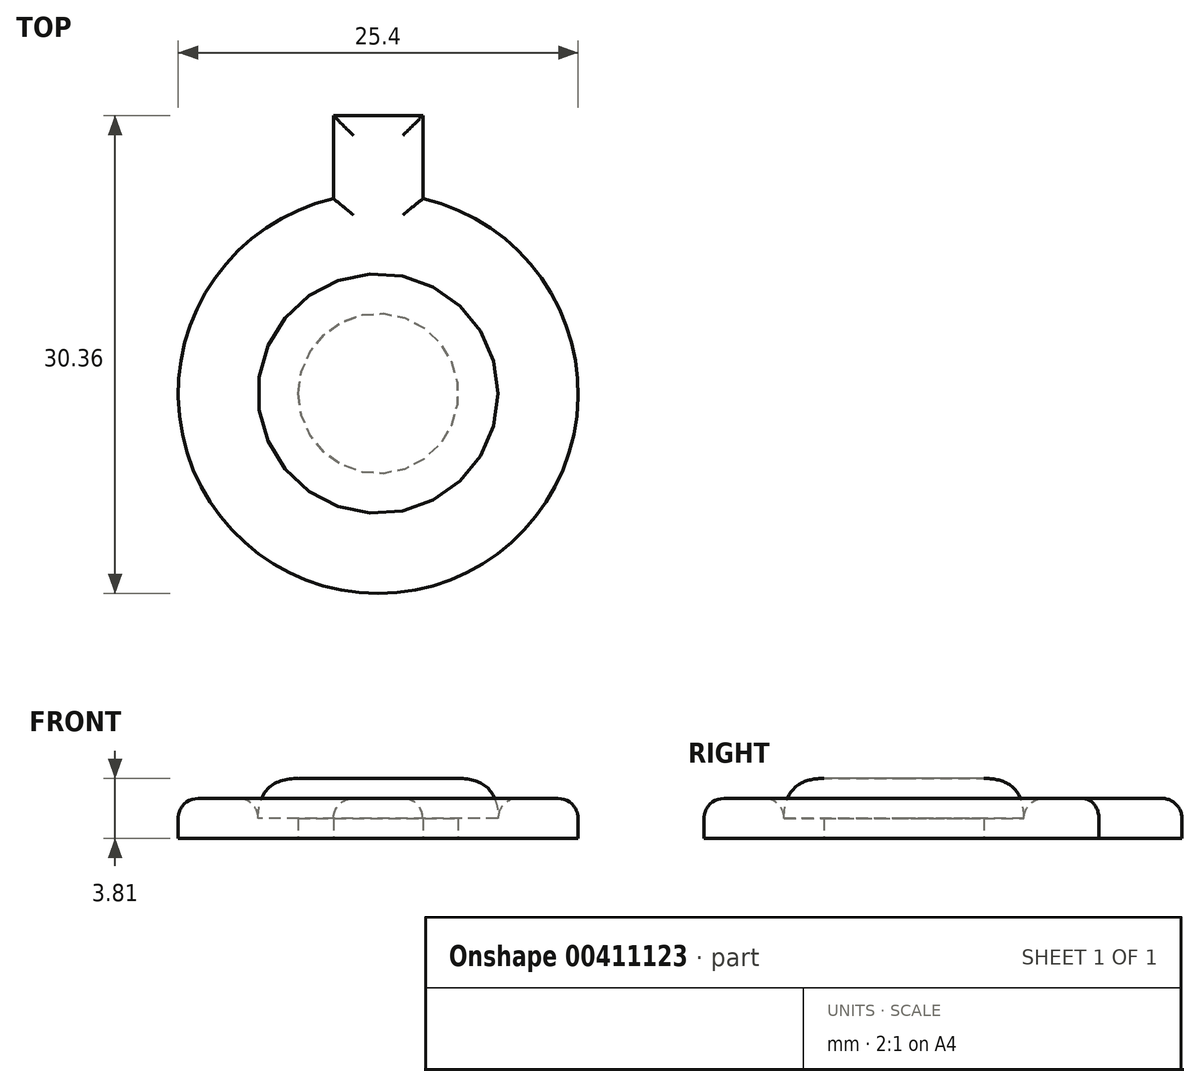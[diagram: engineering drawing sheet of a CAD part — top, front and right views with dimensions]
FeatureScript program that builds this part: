
annotation { "Feature Type Name" : "Feature", "Feature Type Description" : "" }
export const myFeature = defineFeature(function(context is Context, id is Id, definition is map)
    precondition{}
    {
        {
            var Q0;
            Q0=qCreatedBy(makeId("Top.planeOp"),FACE);
            var sketch = newSketch(context, id + "F0", { "sketchPlane" : qUnion([Q0])});
            skCircle(sketch, "E0", {"center": v(0, 0) * mm, "radius": 12.7 * mm});
            skCircle(sketch, "E1.0", {"center": v(0, 0) * mm, "radius": 7.62 * mm});
            skLineSegment(sketch, "E2.bottom", {"start": v(2.84, 17.66) * mm, "end": v(-2.84, 17.66) * mm});
            skLineSegment(sketch, "E2.top", {"start": v(2.84, 7.74) * mm, "end": v(-2.84, 7.74) * mm});
            skLineSegment(sketch, "E2.left", {"start": v(2.84, 17.66) * mm, "end": v(2.84, 7.74) * mm});
            skLineSegment(sketch, "E2.right", {"start": v(-2.84, 17.66) * mm, "end": v(-2.84, 7.74) * mm});
            skPoint(sketch, "E2.middle", {"position": v(0, 12.7) * mm});
            skSolve(sketch);
        }
        {
            var Q0;
            {var subQ5=sQuery(id+"F0.wireOp",EDGE,"E2.top");Q0=makeQuery(id+"F0.imprint","IMPRINT",FACE,{"disambiguationData":[TD([[makeQuery(id+"F0.imprint","IMPRINT",EDGE,{"derivedFrom":subQ5}),-1.0]])]});}
            var Q1;
            {var subQ5=sQuery(id+"F0.wireOp",EDGE,"E2.bottom");Q1=makeQuery(id+"F0.imprint","IMPRINT",FACE,{"disambiguationData":[TD([[makeQuery(id+"F0.imprint","IMPRINT",EDGE,{"derivedFrom":subQ5}),1.0]])]});}
            var Q2;
            Q2=makeQuery(id+"F0.imprint","IMPRINT",FACE,{"disambiguationData":[TD([[makeQuery(id+"F0.imprint","IMPRINT",EDGE,{"derivedFrom":sQuery(id+"F0.wireOp",EDGE,"E1.0")}),-1.0]])]});
            extrude(context, id + "F1", {"entities" : qUnion([Q0, Q1, Q2]), "depth" : 2.54 * mm});
        }
        {
            var Q0;
            Q0=makeQuery(id+"F1.opExtrude","CAP_EDGE",EDGE,{"disambiguationData":[OSD([sQuery(id+"F0.wireOp",EDGE,"E0")])],"isStart":false});
            var Q1;
            Q1=makeQuery(id+"F1.opExtrude","CAP_EDGE",EDGE,{"disambiguationData":[OSD([sQuery(id+"F0.wireOp",EDGE,"E2.left")])],"isStart":false});
            var Q2;
            Q2=makeQuery(id+"F1.opExtrude","CAP_EDGE",EDGE,{"disambiguationData":[OSD([sQuery(id+"F0.wireOp",EDGE,"E2.bottom")])],"isStart":false});
            var Q3;
            Q3=makeQuery(id+"F1.opExtrude","CAP_EDGE",EDGE,{"disambiguationData":[OSD([sQuery(id+"F0.wireOp",EDGE,"E2.right")])],"isStart":false});
            var Q4;
            Q4=makeQuery(id+"F1.opExtrude","CAP_EDGE",EDGE,{"disambiguationData":[OSD([sQuery(id+"F0.wireOp",EDGE,"E1.0")])],"isStart":false});
            fillet(context, id + "F2", {"entities" : qUnion([Q0, Q1, Q2, Q3, Q4]), "radius" : 1.27 * mm, "tangentPropagation" : true, "allowEdgeOverflow" : false});
        }
        {
            var Q0;
            Q0=makeQuery(id+"F0.imprint","IMPRINT",FACE,{"disambiguationData":[TD([[makeQuery(id+"F0.imprint","IMPRINT",EDGE,{"derivedFrom":sQuery(id+"F0.wireOp",EDGE,"E1.0")}),1.0]])]});
            extrude(context, id + "F3", {"entities" : qUnion([Q0]), "operationType" : NewBodyOperationType.ADD, "depth" : 3.8 * mm});
        }
        {
            var Q0;
            Q0=makeQuery(id+"F3.opExtrude","CAP_EDGE",EDGE,{"disambiguationData":[OSD([sQuery(id+"F0.wireOp",EDGE,"E1.0")])],"isStart":false});
            fillet(context, id + "F4", {"entities" : qUnion([Q0]), "radius" : 2.54 * mm, "tangentPropagation" : true, "rho" : 0.5, "crossSection" : FilletCrossSection.CONIC, "allowEdgeOverflow" : false});
        }
        {
            var Q0;
            {var subQ0=sQuery(id+"F0.wireOp",EDGE,"E1.0");Q0=makeQuery(id+"F3.boolean.opBoolean","MERGE",FACE,{"derivedFrom":[makeQuery(id+"F1.opExtrude","CAP_FACE",FACE,{"disambiguationData":[OSD([sQuery(id+"F0.wireOp",EDGE,"E0"),subQ0,sQuery(id+"F0.wireOp",EDGE,"E2.bottom"),sQuery(id+"F0.wireOp",EDGE,"E2.left"),sQuery(id+"F0.wireOp",EDGE,"E2.right")])],"isStart":true}),makeQuery(id+"F3.opExtrude","CAP_FACE",FACE,{"disambiguationData":[OSD([subQ0])],"isStart":true})]});}
            shell(context, id + "F5", {"entities" : qUnion([Q0]), "thickness" : 2.54 * mm});
        }
    });
